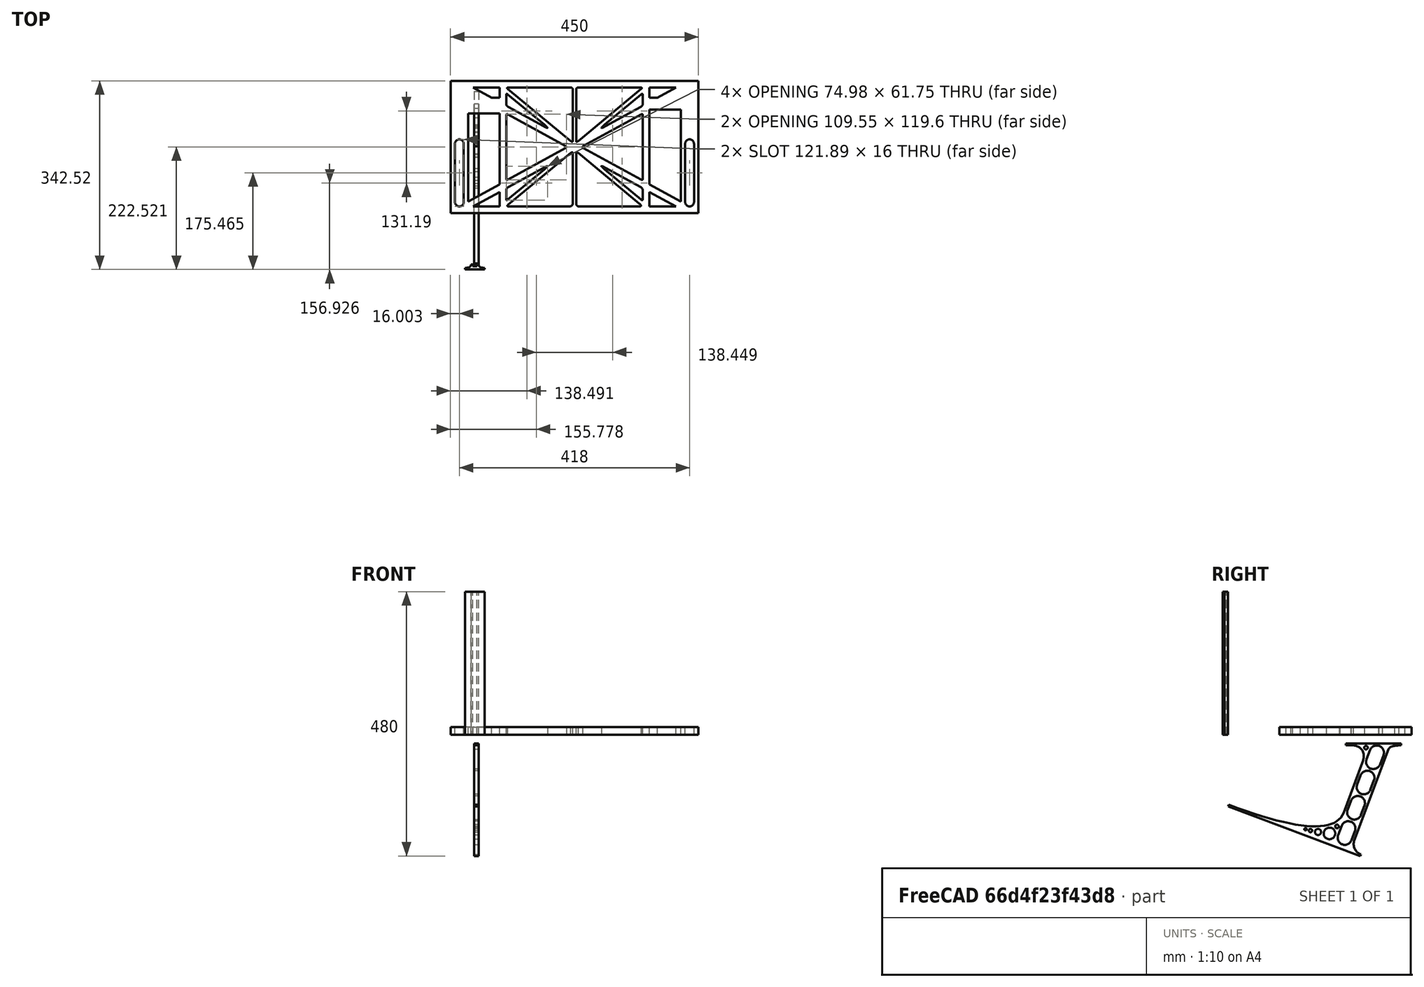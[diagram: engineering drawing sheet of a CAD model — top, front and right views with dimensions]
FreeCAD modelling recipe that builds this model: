
FCSTD DOCUMENT  (FreeCAD 0.19R0.19.2)
Label: laptopStand094
License: All rights reserved
LicenseURL: http://en.wikipedia.org/wiki/All_rights_reserved
objects: Sketcher::SketchObject×3, Part::Extrusion×3
note: 6 computed .brp shape members not serialized (recipe doc carries the construction recipe); baked Part::Feature solids carry a one-line shape summary decoded from their .brp

FEATURE [Sketcher::SketchObject] Sketch
  FullyConstrained = false
  sketch-geometry (252):
    g0: LineSegment StartX=-10.9272 StartY=-82.7794 StartZ=0 EndX=46.0728 EndY=-51.4823 EndZ=0
    g1: LineSegment StartX=366.073 StartY=-91.7794 StartZ=0 EndX=318.073 EndY=-65.424 EndZ=0
    g2: LineSegment StartX=-10.9272 StartY=77.3346 StartZ=0 EndX=-10.9272 EndY=-82.7794 EndZ=0
    g3: LineSegment StartX=375.073 StartY=-82.7794 StartZ=0 EndX=375.073 EndY=83.9235 EndZ=0
    g4: LineSegment StartX=-1.92719 StartY=-91.7794 StartZ=0 EndX=46.0728 EndY=-91.7794 EndZ=0
    g5: LineSegment StartX=318.073 StartY=124.221 StartZ=0 EndX=366.073 EndY=124.221 EndZ=0
    g6: LineSegment StartX=318.073 StartY=83.9235 StartZ=0 EndX=318.073 EndY=-51.4823 EndZ=0
    g7: LineSegment StartX=318.073 StartY=-51.4823 StartZ=0 EndX=375.073 EndY=-82.7794 EndZ=0
    g8: LineSegment StartX=318.073 StartY=-65.424 StartZ=0 EndX=318.073 EndY=-91.7794 EndZ=0
    g9: LineSegment StartX=318.073 StartY=-91.7794 StartZ=0 EndX=366.073 EndY=-91.7794 EndZ=0
    g10: LineSegment StartX=46.0728 StartY=-65.424 StartZ=0 EndX=-1.92719 EndY=-91.7794 EndZ=0
    g11: LineSegment StartX=46.0728 StartY=-65.424 StartZ=0 EndX=46.0728 EndY=-91.7794 EndZ=0
    g12: LineSegment StartX=46.0728 StartY=77.3346 StartZ=0 EndX=46.0728 EndY=-51.4823 EndZ=0
    g13: LineSegment StartX=-42.9272 StartY=136.221 StartZ=0 EndX=-42.9272 EndY=-103.779 EndZ=0
    g14: LineSegment StartX=407.073 StartY=136.221 StartZ=0 EndX=407.073 EndY=-103.779 EndZ=0
    g15: ArcOfCircle CenterX=-26.9272 CenterY=22.1087 CenterZ=0 NormalX=0 NormalY=0 NormalZ=1 AngleXU=0 Radius=8 StartAngle=1e-16 EndAngle=3.14159
    g16: ArcOfCircle CenterX=-26.9272 CenterY=-83.7794 CenterZ=0 NormalX=0 NormalY=0 NormalZ=1 AngleXU=0 Radius=8 StartAngle=3.14159 EndAngle=6.28319
    g17: LineSegment StartX=-34.9272 StartY=22.1087 StartZ=0 EndX=-34.9272 EndY=-83.7794 EndZ=0
    g18: LineSegment StartX=-18.9272 StartY=22.1087 StartZ=0 EndX=-18.9272 EndY=-83.7794 EndZ=0
    g19: ArcOfCircle CenterX=391.073 CenterY=22.1087 CenterZ=0 NormalX=0 NormalY=0 NormalZ=1 AngleXU=0 Radius=8 StartAngle=-4.4e-15 EndAngle=3.14159
    g20: LineSegment StartX=399.073 StartY=22.1087 StartZ=0 EndX=399.073 EndY=-83.7794 EndZ=0
    g21: LineSegment StartX=383.073 StartY=22.1087 StartZ=0 EndX=383.073 EndY=-83.7794 EndZ=0
    g22: ArcOfCircle CenterX=391.073 CenterY=-83.7794 CenterZ=0 NormalX=0 NormalY=0 NormalZ=1 AngleXU=0 Radius=8 StartAngle=3.14159 EndAngle=6.28319
    g23: Circle CenterX=175.022 CenterY=27.0628 CenterZ=0 NormalX=0 NormalY=0 NormalZ=1 AngleXU=0 Radius=1
    g24: Circle CenterX=179.022 CenterY=24.8665 CenterZ=0 NormalX=0 NormalY=0 NormalZ=1 AngleXU=0 Radius=1
    g25: Circle CenterX=179.022 CenterY=27.0628 CenterZ=0 NormalX=0 NormalY=0 NormalZ=1 AngleXU=0 Radius=1
    g26: BSplineCurve PolesCount=3 KnotsCount=2 Degree=2 IsPeriodic=0
    g27: GeomPoint X=175.022 Y=27.0628 Z=0
    g28: GeomPoint X=179.022 Y=27.0628 Z=0
    g29: Circle CenterX=189.124 CenterY=27.0628 CenterZ=0 NormalX=0 NormalY=0 NormalZ=1 AngleXU=0 Radius=1
    g30: Circle CenterX=185.124 CenterY=24.8665 CenterZ=0 NormalX=0 NormalY=0 NormalZ=1 AngleXU=0 Radius=1
    g31: Circle CenterX=185.124 CenterY=27.0628 CenterZ=0 NormalX=0 NormalY=0 NormalZ=1 AngleXU=0 Radius=1
    g32: BSplineCurve PolesCount=3 KnotsCount=2 Degree=2 IsPeriodic=0
    g33: GeomPoint X=189.124 Y=27.0628 Z=0
    g34: GeomPoint X=185.124 Y=27.0628 Z=0
    g35: Circle CenterX=175.022 CenterY=5.37834 CenterZ=0 NormalX=0 NormalY=0 NormalZ=1 AngleXU=0 Radius=1
    g36: Circle CenterX=179.022 CenterY=7.57463 CenterZ=0 NormalX=0 NormalY=0 NormalZ=1 AngleXU=0 Radius=1
    g37: Circle CenterX=179.022 CenterY=5.34704 CenterZ=0 NormalX=0 NormalY=0 NormalZ=1 AngleXU=0 Radius=1
    g38: BSplineCurve PolesCount=3 KnotsCount=2 Degree=2 IsPeriodic=0
    g39: GeomPoint X=175.022 Y=5.37834 Z=0
    g40: GeomPoint X=179.022 Y=5.34704 Z=0
    g41: Circle CenterX=189.124 CenterY=5.37834 CenterZ=0 NormalX=0 NormalY=0 NormalZ=1 AngleXU=0 Radius=1
    g42: Circle CenterX=185.124 CenterY=7.57463 CenterZ=0 NormalX=0 NormalY=0 NormalZ=1 AngleXU=0 Radius=1
    g43: Circle CenterX=185.124 CenterY=5.34704 CenterZ=0 NormalX=0 NormalY=0 NormalZ=1 AngleXU=0 Radius=1
    g44: BSplineCurve PolesCount=3 KnotsCount=2 Degree=2 IsPeriodic=0
    g45: GeomPoint X=189.124 Y=5.37834 Z=0
    g46: GeomPoint X=185.124 Y=5.34704 Z=0
    g47: Circle CenterX=165.871 CenterY=18.1458 CenterZ=0 NormalX=0 NormalY=0 NormalZ=1 AngleXU=0 Radius=1
    g48: Circle CenterX=169.377 CenterY=16.2206 CenterZ=0 NormalX=0 NormalY=0 NormalZ=1 AngleXU=0 Radius=1
    g49: Circle CenterX=165.871 CenterY=14.2954 CenterZ=0 NormalX=0 NormalY=0 NormalZ=1 AngleXU=0 Radius=1
    g50: BSplineCurve PolesCount=3 KnotsCount=2 Degree=2 IsPeriodic=0
    g51: GeomPoint X=165.871 Y=18.1458 Z=0
    g52: GeomPoint X=165.871 Y=14.2954 Z=0
    g53: Circle CenterX=198.275 CenterY=18.1458 CenterZ=0 NormalX=0 NormalY=0 NormalZ=1 AngleXU=0 Radius=1
    g54: Circle CenterX=194.768 CenterY=16.2206 CenterZ=0 NormalX=0 NormalY=0 NormalZ=1 AngleXU=0 Radius=1
    g55: Circle CenterX=198.275 CenterY=14.2954 CenterZ=0 NormalX=0 NormalY=0 NormalZ=1 AngleXU=0 Radius=1
    g56: BSplineCurve PolesCount=3 KnotsCount=2 Degree=2 IsPeriodic=0
    g57: GeomPoint X=198.275 Y=18.1458 Z=0
    g58: GeomPoint X=198.275 Y=14.2954 Z=0
    g59: LineSegment StartX=407.073 StartY=-103.779 StartZ=0 EndX=-42.9272 EndY=-103.779 EndZ=0
    g60: LineSegment StartX=407.073 StartY=136.221 StartZ=0 EndX=-42.9272 EndY=136.221 EndZ=0
    g61: LineSegment StartX=46.0728 StartY=77.3346 StartZ=0 EndX=-10.9272 EndY=77.3346 EndZ=0
    g62: LineSegment StartX=46.0728 StartY=105.865 StartZ=0 EndX=31.5028 EndY=105.865 EndZ=0
    g63: LineSegment StartX=46.0728 StartY=124.221 StartZ=0 EndX=46.0728 EndY=105.865 EndZ=0
    g64: LineSegment StartX=-1.92719 StartY=124.221 StartZ=0 EndX=31.5028 EndY=105.865 EndZ=0
    g65: LineSegment StartX=46.0728 StartY=124.221 StartZ=0 EndX=-1.92719 EndY=124.221 EndZ=0
    g66: LineSegment StartX=318.073 StartY=83.9235 StartZ=0 EndX=375.073 EndY=83.9235 EndZ=0
    g67: LineSegment StartX=318.073 StartY=105.865 StartZ=0 EndX=332.643 EndY=105.865 EndZ=0
    g68: LineSegment StartX=332.643 StartY=105.865 StartZ=0 EndX=366.073 EndY=124.221 EndZ=0
    g69: LineSegment StartX=318.073 StartY=124.221 StartZ=0 EndX=318.073 EndY=105.865 EndZ=0
    g70: Circle CenterX=125.607 CenterY=54.1951 CenterZ=0 NormalX=0 NormalY=0 NormalZ=1 AngleXU=0 Radius=1
    g71: Circle CenterX=139.632 CenterY=46.4944 CenterZ=0 NormalX=0 NormalY=0 NormalZ=1 AngleXU=0 Radius=1
    g72: Circle CenterX=127.326 CenterY=56.7187 CenterZ=0 NormalX=0 NormalY=0 NormalZ=1 AngleXU=0 Radius=1
    g73: BSplineCurve PolesCount=3 KnotsCount=2 Degree=2 IsPeriodic=0
    g74: GeomPoint X=125.607 Y=54.1951 Z=0
    g75: GeomPoint X=127.326 Y=56.7187 Z=0
    g76: Circle CenterX=236.821 CenterY=56.7187 CenterZ=0 NormalX=0 NormalY=0 NormalZ=1 AngleXU=0 Radius=1
    g77: Circle CenterX=224.513 CenterY=46.4944 CenterZ=0 NormalX=0 NormalY=0 NormalZ=1 AngleXU=0 Radius=1
    g78: Circle CenterX=238.538 CenterY=54.1951 CenterZ=0 NormalX=0 NormalY=0 NormalZ=1 AngleXU=0 Radius=1
    g79: BSplineCurve PolesCount=3 KnotsCount=2 Degree=2 IsPeriodic=0
    g80: GeomPoint X=236.821 Y=56.7187 Z=0
    g81: GeomPoint X=238.538 Y=54.1951 Z=0
    g82: Circle CenterX=238.538 CenterY=-21.7539 CenterZ=0 NormalX=0 NormalY=0 NormalZ=1 AngleXU=0 Radius=1
    g83: Circle CenterX=224.513 CenterY=-14.0532 CenterZ=0 NormalX=0 NormalY=0 NormalZ=1 AngleXU=0 Radius=1
    g84: Circle CenterX=236.821 CenterY=-24.2775 CenterZ=0 NormalX=0 NormalY=0 NormalZ=1 AngleXU=0 Radius=1
    g85: BSplineCurve PolesCount=3 KnotsCount=2 Degree=2 IsPeriodic=0
    g86: GeomPoint X=238.538 Y=-21.7539 Z=0
    g87: GeomPoint X=236.821 Y=-24.2775 Z=0
    g88: Circle CenterX=125.607 CenterY=-21.7539 CenterZ=0 NormalX=0 NormalY=0 NormalZ=1 AngleXU=0 Radius=1
    g89: Circle CenterX=139.632 CenterY=-14.0532 CenterZ=0 NormalX=0 NormalY=0 NormalZ=1 AngleXU=0 Radius=1
    g90: Circle CenterX=127.325 CenterY=-24.2775 CenterZ=0 NormalX=0 NormalY=0 NormalZ=1 AngleXU=0 Radius=1
    g91: BSplineCurve PolesCount=3 KnotsCount=2 Degree=2 IsPeriodic=0
    g92: GeomPoint X=125.607 Y=-21.7539 Z=0
    g93: GeomPoint X=127.325 Y=-24.2775 Z=0
    g94: Circle CenterX=302.996 CenterY=111.695 CenterZ=0 NormalX=0 NormalY=0 NormalZ=1 AngleXU=0 Radius=1
    g95: Circle CenterX=306.073 CenterY=114.251 CenterZ=0 NormalX=0 NormalY=0 NormalZ=1 AngleXU=0 Radius=1
    g96: Circle CenterX=306.073 CenterY=110.251 CenterZ=0 NormalX=0 NormalY=0 NormalZ=1 AngleXU=0 Radius=1
    g97: BSplineCurve PolesCount=3 KnotsCount=2 Degree=2 IsPeriodic=0
    g98: GeomPoint X=302.996 Y=111.695 Z=0
    g99: GeomPoint X=306.073 Y=110.251 Z=0
    g100: Circle CenterX=306.073 CenterY=95.2763 CenterZ=0 NormalX=0 NormalY=0 NormalZ=1 AngleXU=0 Radius=1
    g101: Circle CenterX=306.073 CenterY=91.2763 CenterZ=0 NormalX=0 NormalY=0 NormalZ=1 AngleXU=0 Radius=1
    g102: Circle CenterX=302.567 CenterY=89.3511 CenterZ=0 NormalX=0 NormalY=0 NormalZ=1 AngleXU=0 Radius=1
    g103: BSplineCurve PolesCount=3 KnotsCount=2 Degree=2 IsPeriodic=0
    g104: GeomPoint X=306.073 Y=95.2763 Z=0
    g105: GeomPoint X=302.567 Y=89.3511 Z=0
    g106: LineSegment StartX=306.073 StartY=110.251 StartZ=0 EndX=306.073 EndY=95.2763 EndZ=0
    g107: LineSegment StartX=302.996 StartY=111.695 StartZ=0 EndX=236.821 EndY=56.7187 EndZ=0
    g108: LineSegment StartX=238.538 StartY=54.1951 StartZ=0 EndX=302.567 EndY=89.3511 EndZ=0
    g109: Circle CenterX=61.1496 CenterY=111.695 CenterZ=0 NormalX=0 NormalY=0 NormalZ=1 AngleXU=0 Radius=1
    g110: Circle CenterX=58.0728 CenterY=114.251 CenterZ=0 NormalX=0 NormalY=0 NormalZ=1 AngleXU=0 Radius=1
    g111: Circle CenterX=58.0728 CenterY=110.251 CenterZ=0 NormalX=0 NormalY=0 NormalZ=1 AngleXU=0 Radius=1
    g112: BSplineCurve PolesCount=3 KnotsCount=2 Degree=2 IsPeriodic=0
    g113: GeomPoint X=61.1496 Y=111.695 Z=0
    g114: GeomPoint X=58.0728 Y=110.251 Z=0
    g115: Circle CenterX=61.5791 CenterY=89.3511 CenterZ=0 NormalX=0 NormalY=0 NormalZ=1 AngleXU=0 Radius=1
    g116: Circle CenterX=58.0728 CenterY=91.2763 CenterZ=0 NormalX=0 NormalY=0 NormalZ=1 AngleXU=0 Radius=1
    g117: Circle CenterX=58.0728 CenterY=95.2763 CenterZ=0 NormalX=0 NormalY=0 NormalZ=1 AngleXU=0 Radius=1
    g118: BSplineCurve PolesCount=3 KnotsCount=2 Degree=2 IsPeriodic=0
    g119: GeomPoint X=61.5791 Y=89.3511 Z=0
    g120: GeomPoint X=58.0728 Y=95.2763 Z=0
    g121: LineSegment StartX=58.0728 StartY=110.251 StartZ=0 EndX=58.0728 EndY=95.2763 EndZ=0
    g122: LineSegment StartX=61.1496 StartY=111.695 StartZ=0 EndX=127.326 EndY=56.7187 EndZ=0
    g123: LineSegment StartX=125.607 StartY=54.1951 StartZ=0 EndX=61.5791 EndY=89.3511 EndZ=0
    g124: Circle CenterX=61.5791 CenterY=-56.9099 CenterZ=0 NormalX=0 NormalY=0 NormalZ=1 AngleXU=0 Radius=1
    g125: Circle CenterX=58.0728 CenterY=-58.8351 CenterZ=0 NormalX=0 NormalY=0 NormalZ=1 AngleXU=0 Radius=1
    g126: Circle CenterX=58.0728 CenterY=-62.8351 CenterZ=0 NormalX=0 NormalY=0 NormalZ=1 AngleXU=0 Radius=1
    g127: BSplineCurve PolesCount=3 KnotsCount=2 Degree=2 IsPeriodic=0
    g128: GeomPoint X=61.5791 Y=-56.9099 Z=0
    g129: GeomPoint X=58.0728 Y=-62.8351 Z=0
    g130: Circle CenterX=58.0728 CenterY=-77.8102 CenterZ=0 NormalX=0 NormalY=0 NormalZ=1 AngleXU=0 Radius=1
    g131: Circle CenterX=58.0728 CenterY=-81.8102 CenterZ=0 NormalX=0 NormalY=0 NormalZ=1 AngleXU=0 Radius=1
    g132: Circle CenterX=61.1496 CenterY=-79.2541 CenterZ=0 NormalX=0 NormalY=0 NormalZ=1 AngleXU=0 Radius=1
    g133: BSplineCurve PolesCount=3 KnotsCount=2 Degree=2 IsPeriodic=0
    g134: GeomPoint X=58.0728 Y=-77.8102 Z=0
    g135: GeomPoint X=61.1496 Y=-79.2541 Z=0
    g136: LineSegment StartX=58.0728 StartY=-62.8351 StartZ=0 EndX=58.0728 EndY=-77.8102 EndZ=0
    g137: LineSegment StartX=61.1496 StartY=-79.2541 StartZ=0 EndX=127.325 EndY=-24.2775 EndZ=0
    g138: LineSegment StartX=125.607 StartY=-21.7539 StartZ=0 EndX=61.5791 EndY=-56.9099 EndZ=0
    g139: Circle CenterX=302.567 CenterY=-56.9099 CenterZ=0 NormalX=0 NormalY=0 NormalZ=1 AngleXU=0 Radius=1
    g140: Circle CenterX=306.073 CenterY=-58.8351 CenterZ=0 NormalX=0 NormalY=0 NormalZ=1 AngleXU=0 Radius=1
    g141: Circle CenterX=306.073 CenterY=-62.8351 CenterZ=0 NormalX=0 NormalY=0 NormalZ=1 AngleXU=0 Radius=1
    g142: BSplineCurve PolesCount=3 KnotsCount=2 Degree=2 IsPeriodic=0
    g143: GeomPoint X=302.567 Y=-56.9099 Z=0
    g144: GeomPoint X=306.073 Y=-62.8351 Z=0
    g145: Circle CenterX=302.996 CenterY=-79.2541 CenterZ=0 NormalX=0 NormalY=0 NormalZ=1 AngleXU=0 Radius=1
    g146: Circle CenterX=306.073 CenterY=-81.8102 CenterZ=0 NormalX=0 NormalY=0 NormalZ=1 AngleXU=0 Radius=1
    g147: Circle CenterX=306.073 CenterY=-77.8102 CenterZ=0 NormalX=0 NormalY=0 NormalZ=1 AngleXU=0 Radius=1
    g148: BSplineCurve PolesCount=3 KnotsCount=2 Degree=2 IsPeriodic=0
    g149: GeomPoint X=302.996 Y=-79.2541 Z=0
    g150: GeomPoint X=306.073 Y=-77.8102 Z=0
    g151: LineSegment StartX=306.073 StartY=-62.8351 StartZ=0 EndX=306.073 EndY=-77.8102 EndZ=0
    g152: LineSegment StartX=302.996 StartY=-79.2541 StartZ=0 EndX=236.821 EndY=-24.2775 EndZ=0
    g153: LineSegment StartX=238.538 StartY=-21.7539 StartZ=0 EndX=302.567 EndY=-56.9099 EndZ=0
    g154: Circle CenterX=61.6457 CenterY=-88.8112 CenterZ=0 NormalX=0 NormalY=0 NormalZ=1 AngleXU=0 Radius=1
    g155: Circle CenterX=58.0728 CenterY=-91.7794 CenterZ=0 NormalX=0 NormalY=0 NormalZ=1 AngleXU=0 Radius=1
    g156: Circle CenterX=63.9135 CenterY=-91.7794 CenterZ=0 NormalX=0 NormalY=0 NormalZ=1 AngleXU=0 Radius=1
    g157: BSplineCurve PolesCount=3 KnotsCount=2 Degree=2 IsPeriodic=0
    g158: GeomPoint X=61.6457 Y=-88.8112 Z=0
    g159: GeomPoint X=63.9135 Y=-91.7794 Z=0
    g160: Circle CenterX=179.022 CenterY=-85.8163 CenterZ=0 NormalX=0 NormalY=0 NormalZ=1 AngleXU=0 Radius=1
    g161: Circle CenterX=179.022 CenterY=-91.7794 CenterZ=0 NormalX=0 NormalY=0 NormalZ=1 AngleXU=0 Radius=1
    g162: Circle CenterX=171.895 CenterY=-91.7794 CenterZ=0 NormalX=0 NormalY=0 NormalZ=1 AngleXU=0 Radius=1
    g163: BSplineCurve PolesCount=3 KnotsCount=2 Degree=2 IsPeriodic=0
    g164: GeomPoint X=179.022 Y=-85.8163 Z=0
    g165: GeomPoint X=171.895 Y=-91.7794 Z=0
    g166: Circle CenterX=185.124 CenterY=-86.2028 CenterZ=0 NormalX=0 NormalY=0 NormalZ=1 AngleXU=0 Radius=1
    g167: Circle CenterX=185.124 CenterY=-91.7794 CenterZ=0 NormalX=0 NormalY=0 NormalZ=1 AngleXU=0 Radius=1
    g168: Circle CenterX=191.747 CenterY=-91.7794 CenterZ=0 NormalX=0 NormalY=0 NormalZ=1 AngleXU=0 Radius=1
    g169: BSplineCurve PolesCount=3 KnotsCount=2 Degree=2 IsPeriodic=0
    g170: GeomPoint X=185.124 Y=-86.2028 Z=0
    g171: GeomPoint X=191.747 Y=-91.7794 Z=0
    g172: Circle CenterX=299.888 CenterY=-86.6413 CenterZ=0 NormalX=0 NormalY=0 NormalZ=1 AngleXU=0 Radius=1
    g173: Circle CenterX=306.073 CenterY=-91.7794 CenterZ=0 NormalX=0 NormalY=0 NormalZ=1 AngleXU=0 Radius=1
    g174: Circle CenterX=298.776 CenterY=-91.7794 CenterZ=0 NormalX=0 NormalY=0 NormalZ=1 AngleXU=0 Radius=1
    g175: BSplineCurve PolesCount=3 KnotsCount=2 Degree=2 IsPeriodic=0
    g176: GeomPoint X=299.888 Y=-86.6413 Z=0
    g177: GeomPoint X=298.776 Y=-91.7794 Z=0
    g178: LineSegment StartX=189.124 StartY=5.37834 StartZ=0 EndX=299.888 EndY=-86.6413 EndZ=0
    g179: LineSegment StartX=298.776 StartY=-91.7794 StartZ=0 EndX=191.747 EndY=-91.7794 EndZ=0
    g180: LineSegment StartX=185.124 StartY=-86.2028 StartZ=0 EndX=185.124 EndY=5.34704 EndZ=0
    g181: LineSegment StartX=179.022 StartY=5.34704 StartZ=0 EndX=179.022 EndY=-85.8163 EndZ=0
    g182: LineSegment StartX=171.895 StartY=-91.7794 StartZ=0 EndX=63.9135 EndY=-91.7794 EndZ=0
    g183: LineSegment StartX=61.6457 StartY=-88.8112 StartZ=0 EndX=175.022 EndY=5.37834 EndZ=0
    g184: Circle CenterX=302.073 CenterY=124.221 CenterZ=0 NormalX=0 NormalY=0 NormalZ=1 AngleXU=0 Radius=1
    g185: Circle CenterX=306.073 CenterY=124.221 CenterZ=0 NormalX=0 NormalY=0 NormalZ=1 AngleXU=0 Radius=1
    g186: Circle CenterX=302.996 CenterY=121.665 CenterZ=0 NormalX=0 NormalY=0 NormalZ=1 AngleXU=0 Radius=1
    g187: BSplineCurve PolesCount=3 KnotsCount=2 Degree=2 IsPeriodic=0
    g188: GeomPoint X=302.073 Y=124.221 Z=0
    g189: GeomPoint X=302.996 Y=121.665 Z=0
    g190: Circle CenterX=189.124 CenterY=124.221 CenterZ=0 NormalX=0 NormalY=0 NormalZ=1 AngleXU=0 Radius=1
    g191: Circle CenterX=185.124 CenterY=124.221 CenterZ=0 NormalX=0 NormalY=0 NormalZ=1 AngleXU=0 Radius=1
    g192: Circle CenterX=185.124 CenterY=120.221 CenterZ=0 NormalX=0 NormalY=0 NormalZ=1 AngleXU=0 Radius=1
    g193: BSplineCurve PolesCount=3 KnotsCount=2 Degree=2 IsPeriodic=0
    g194: GeomPoint X=189.124 Y=124.221 Z=0
    g195: GeomPoint X=185.124 Y=120.221 Z=0
    g196: Circle CenterX=175.022 CenterY=124.221 CenterZ=0 NormalX=0 NormalY=0 NormalZ=1 AngleXU=0 Radius=1
    g197: Circle CenterX=179.022 CenterY=124.221 CenterZ=0 NormalX=0 NormalY=0 NormalZ=1 AngleXU=0 Radius=1
    g198: Circle CenterX=179.022 CenterY=120.221 CenterZ=0 NormalX=0 NormalY=0 NormalZ=1 AngleXU=0 Radius=1
    g199: BSplineCurve PolesCount=3 KnotsCount=2 Degree=2 IsPeriodic=0
    g200: GeomPoint X=175.022 Y=124.221 Z=0
    g201: GeomPoint X=179.022 Y=120.221 Z=0
    g202: Circle CenterX=62.0728 CenterY=124.221 CenterZ=0 NormalX=0 NormalY=0 NormalZ=1 AngleXU=0 Radius=1
    g203: Circle CenterX=58.0728 CenterY=124.221 CenterZ=0 NormalX=0 NormalY=0 NormalZ=1 AngleXU=0 Radius=1
    g204: Circle CenterX=61.1496 CenterY=121.665 CenterZ=0 NormalX=0 NormalY=0 NormalZ=1 AngleXU=0 Radius=1
    g205: BSplineCurve PolesCount=3 KnotsCount=2 Degree=2 IsPeriodic=0
    g206: GeomPoint X=62.0728 Y=124.221 Z=0
    g207: GeomPoint X=61.1496 Y=121.665 Z=0
    g208: LineSegment StartX=62.0728 StartY=124.221 StartZ=0 EndX=175.022 EndY=124.221 EndZ=0
    g209: LineSegment StartX=179.022 StartY=120.221 StartZ=0 EndX=179.022 EndY=27.0628 EndZ=0
    g210: LineSegment StartX=185.124 StartY=27.0628 StartZ=0 EndX=185.124 EndY=120.221 EndZ=0
    g211: LineSegment StartX=189.124 StartY=124.221 StartZ=0 EndX=302.073 EndY=124.221 EndZ=0
    g212: LineSegment StartX=302.996 StartY=121.665 StartZ=0 EndX=189.124 EndY=27.0628 EndZ=0
    g213: LineSegment StartX=175.022 StartY=27.0628 StartZ=0 EndX=61.1496 EndY=121.665 EndZ=0
    g214: Circle CenterX=61.5791 CenterY=75.4095 CenterZ=0 NormalX=0 NormalY=0 NormalZ=1 AngleXU=0 Radius=1
    g215: Circle CenterX=58.0728 CenterY=77.3346 CenterZ=0 NormalX=0 NormalY=0 NormalZ=1 AngleXU=0 Radius=1
    g216: Circle CenterX=58.0728 CenterY=73.3346 CenterZ=0 NormalX=0 NormalY=0 NormalZ=1 AngleXU=0 Radius=1
    g217: BSplineCurve PolesCount=3 KnotsCount=2 Degree=2 IsPeriodic=0
    g218: GeomPoint X=61.5791 Y=75.4095 Z=0
    g219: GeomPoint X=58.0728 Y=73.3346 Z=0
    g220: Circle CenterX=58.0728 CenterY=-40.8935 CenterZ=0 NormalX=0 NormalY=0 NormalZ=1 AngleXU=0 Radius=1
    g221: Circle CenterX=58.0728 CenterY=-44.8935 CenterZ=0 NormalX=0 NormalY=0 NormalZ=1 AngleXU=0 Radius=1
    g222: Circle CenterX=61.5791 CenterY=-42.9683 CenterZ=0 NormalX=0 NormalY=0 NormalZ=1 AngleXU=0 Radius=1
    g223: BSplineCurve PolesCount=3 KnotsCount=2 Degree=2 IsPeriodic=0
    g224: GeomPoint X=58.0728 Y=-40.8935 Z=0
    g225: GeomPoint X=61.5791 Y=-42.9683 Z=0
    g226: LineSegment StartX=61.5791 StartY=-42.9683 StartZ=0 EndX=165.871 EndY=14.2954 EndZ=0
    g227: LineSegment StartX=165.871 StartY=18.1458 StartZ=0 EndX=61.5791 EndY=75.4095 EndZ=0
    g228: LineSegment StartX=58.0728 StartY=73.3346 StartZ=0 EndX=58.0728 EndY=-40.8935 EndZ=0
    g229: Circle CenterX=302.567 CenterY=-42.9683 CenterZ=0 NormalX=0 NormalY=0 NormalZ=1 AngleXU=0 Radius=1
    g230: Circle CenterX=306.073 CenterY=-44.8935 CenterZ=0 NormalX=0 NormalY=0 NormalZ=1 AngleXU=0 Radius=1
    g231: Circle CenterX=306.073 CenterY=-40.8935 CenterZ=0 NormalX=0 NormalY=0 NormalZ=1 AngleXU=0 Radius=1
    g232: BSplineCurve PolesCount=3 KnotsCount=2 Degree=2 IsPeriodic=0
    g233: GeomPoint X=302.567 Y=-42.9683 Z=0
    g234: GeomPoint X=306.073 Y=-40.8935 Z=0
    g235: Circle CenterX=306.073 CenterY=73.3346 CenterZ=0 NormalX=0 NormalY=0 NormalZ=1 AngleXU=0 Radius=1
    g236: Circle CenterX=306.073 CenterY=77.3346 CenterZ=0 NormalX=0 NormalY=0 NormalZ=1 AngleXU=0 Radius=1
    g237: Circle CenterX=302.567 CenterY=75.4095 CenterZ=0 NormalX=0 NormalY=0 NormalZ=1 AngleXU=0 Radius=1
    g238: BSplineCurve PolesCount=3 KnotsCount=2 Degree=2 IsPeriodic=0
    g239: GeomPoint X=306.073 Y=73.3346 Z=0
    g240: GeomPoint X=302.567 Y=75.4095 Z=0
    g241: LineSegment StartX=302.567 StartY=-42.9683 StartZ=0 EndX=198.275 EndY=14.2954 EndZ=0
    g242: LineSegment StartX=198.275 StartY=18.1458 StartZ=0 EndX=302.567 EndY=75.4095 EndZ=0
    g243: LineSegment StartX=306.073 StartY=73.3346 StartZ=0 EndX=306.073 EndY=-40.8935 EndZ=0
    g244: LineSegment StartX=318.073 StartY=124.221 StartZ=0 EndX=322.073 EndY=124.221 EndZ=0
    g245: LineSegment StartX=366.073 StartY=124.221 StartZ=0 EndX=362.073 EndY=124.221 EndZ=0
    g246: LineSegment StartX=328.643 StartY=105.865 StartZ=0 EndX=332.643 EndY=105.865 EndZ=0
    g247: LineSegment StartX=335.6 StartY=105.351 StartZ=0 EndX=339.311 EndY=107.624 EndZ=0
    g248: LineSegment StartX=366.554 StartY=122.928 StartZ=0 EndX=363.62 EndY=120.771 EndZ=0
    g249: LineSegment StartX=318.073 StartY=105.865 StartZ=0 EndX=318.073 EndY=109.865 EndZ=0
    g250: LineSegment StartX=318.073 StartY=105.865 StartZ=0 EndX=322.073 EndY=105.865 EndZ=0
    g251: LineSegment StartX=318.073 StartY=124.221 StartZ=0 EndX=318.073 EndY=120.221 EndZ=0
  constraints (433):
    c: Horizontal(g4)
    c: Horizontal(g5)
    c: Coincident(g6,g7)
    c: Coincident(g8,g1)
    c: Tangent(g6,g8)
    c: Coincident(g11,g10)
    c: Coincident(g0,g12)
    c: Block(g7)
    c: Block(g3)
    c: Block(g1)
    c: Block(g8)
    c: Block(g11)
    c: Block(g10)
    c: Block(g0)
    c: Block(g2)
    c: Block(g5)
    c: Block(g9)
    c: Block(g4)
    c: Vertical(g13)
    c: Vertical(g14)
    c: Block(g14)
    c: Block(g13)
    c: Tangent(g15,g18) = 1.5708
    c: Tangent(g15,g17) = -1.5708
    c: Tangent(g17,g16) = -1.5708
    c: Tangent(g18,g16) = 1.5708
    c: Vertical(g17)
    c: Equal(g15,g16)
    c: Block(g18)
    c: Block(g17)
    c: Tangent(g19,g20) = 1.5708
    c: Tangent(g20,g22) = 1.5708
    c: Equal(g19,g22)
    c: Coincident(g21,g19)
    c: Coincident(g21,g22)
    c: Block(g20)
    c: Block(g21)
    c: Weight(g23) = 1
    c: Equal(g23,g24)
    c: Equal(g23,g25)
    c: InternalAlignment(g23,g26)
    c: InternalAlignment(g24,g26)
    c: InternalAlignment(g25,g26)
    c: InternalAlignment(g27,g26)
    c: InternalAlignment(g28,g26)
    c: Weight(g29) = 1
    c: Equal(g29,g30)
    c: Equal(g29,g31)
    c: InternalAlignment(g29,g32)
    c: InternalAlignment(g30,g32)
    c: InternalAlignment(g31,g32)
    c: InternalAlignment(g33,g32)
    c: InternalAlignment(g34,g32)
    c: Block(g32)
    c: Block(g26)
    c: Weight(g35) = 1
    c: Equal(g35,g36)
    c: Equal(g35,g37)
    c: InternalAlignment(g35,g38)
    c: InternalAlignment(g36,g38)
    c: InternalAlignment(g37,g38)
    c: InternalAlignment(g39,g38)
    c: InternalAlignment(g40,g38)
    c: Weight(g41) = 1
    c: Equal(g41,g42)
    c: Equal(g41,g43)
    c: InternalAlignment(g41,g44)
    c: InternalAlignment(g42,g44)
    c: InternalAlignment(g43,g44)
    c: InternalAlignment(g45,g44)
    c: InternalAlignment(g46,g44)
    c: Block(g44)
    c: Block(g38)
    c: Weight(g47) = 1
    c: Equal(g47,g48)
    c: Equal(g47,g49)
    c: InternalAlignment(g47,g50)
    c: InternalAlignment(g48,g50)
    c: InternalAlignment(g49,g50)
    c: InternalAlignment(g51,g50)
    c: InternalAlignment(g52,g50)
    c: Weight(g53) = 1
    c: Equal(g53,g54)
    c: Equal(g53,g55)
    c: InternalAlignment(g53,g56)
    c: InternalAlignment(g54,g56)
    c: InternalAlignment(g55,g56)
    c: InternalAlignment(g57,g56)
    c: InternalAlignment(g58,g56)
    c: Block(g50)
    c: Block(g56)
    c: Coincident(g59,g14)
    c: Coincident(g59,g13)
    c: Horizontal(g59)
    c: Distance(g59) = 450
    c: Coincident(g60,g14)
    c: Coincident(g60,g13)
    c: Horizontal(g60)
    c: Horizontal(g61)
    c: Coincident(g12,g61)
    c: Horizontal(g62)
    c: Vertical(g63)
    c: Block(g63)
    c: Block(g62)
    c: Block(g61)
    c: Distance(g63) = 18.3554
    c: Coincident(g65,g63)
    c: Coincident(g65,g64)
    c: Horizontal(g65)
    c: Block(g65)
    c: Block(g64)
    c: Coincident(g62,g64)
    c: Coincident(g2,g61)
    c: Coincident(g66,g6)
    c: Horizontal(g66)
    c: Horizontal(g67)
    c: Block(g66)
    c: Coincident(g68,g5)
    c: Coincident(g69,g5)
    c: Coincident(g69,g67)
    c: Vertical(g69)
    c: Block(g69)
    c: Coincident(g67,g68)
    c: Block(g68)
    c: Coincident(g3,g66)
    c: Weight(g70) = 1
    c: Equal(g70,g71)
    c: Equal(g70,g72)
    c: InternalAlignment(g70,g73)
    c: InternalAlignment(g71,g73)
    c: InternalAlignment(g72,g73)
    c: InternalAlignment(g74,g73)
    c: InternalAlignment(g75,g73)
    c: Block(g73)
    c: Weight(g76) = 1
    c: Equal(g76,g77)
    c: Equal(g76,g78)
    c: InternalAlignment(g76,g79)
    c: InternalAlignment(g77,g79)
    c: InternalAlignment(g78,g79)
    c: InternalAlignment(g80,g79)
    c: InternalAlignment(g81,g79)
    c: Block(g79)
    c: Weight(g82) = 1
    c: Equal(g82,g83)
    c: Equal(g82,g84)
    c: InternalAlignment(g82,g85)
    c: InternalAlignment(g83,g85)
    c: InternalAlignment(g84,g85)
    c: InternalAlignment(g86,g85)
    c: InternalAlignment(g87,g85)
    c: Block(g85)
    c: Weight(g88) = 1
    c: Equal(g88,g89)
    c: Equal(g88,g90)
    c: InternalAlignment(g88,g91)
    c: InternalAlignment(g89,g91)
    c: InternalAlignment(g90,g91)
    c: InternalAlignment(g92,g91)
    c: InternalAlignment(g93,g91)
    c: Block(g91)
    c: Weight(g94) = 1
    c: Equal(g94,g95)
    c: Equal(g94,g96)
    c: InternalAlignment(g94,g97)
    c: InternalAlignment(g95,g97)
    c: InternalAlignment(g96,g97)
    c: InternalAlignment(g98,g97)
    c: InternalAlignment(g99,g97)
    c: Weight(g100) = 1
    c: Equal(g100,g101)
    c: Equal(g100,g102)
    c: InternalAlignment(g100,g103)
    c: InternalAlignment(g101,g103)
    c: InternalAlignment(g102,g103)
    c: InternalAlignment(g104,g103)
    c: InternalAlignment(g105,g103)
    c: Block(g97)
    c: Block(g103)
    c: Coincident(g106,g97)
    c: Coincident(g106,g103)
    c: Vertical(g106)
    c: Coincident(g107,g97)
    c: Coincident(g107,g79)
    c: Coincident(g108,g79)
    c: Coincident(g108,g103)
    c: Weight(g109) = 1
    c: Equal(g109,g110)
    c: Equal(g109,g111)
    c: InternalAlignment(g109,g112)
    c: InternalAlignment(g110,g112)
    c: InternalAlignment(g111,g112)
    c: InternalAlignment(g113,g112)
    c: InternalAlignment(g114,g112)
    c: Weight(g115) = 1
    c: Equal(g115,g116)
    c: Equal(g115,g117)
    c: InternalAlignment(g115,g118)
    c: InternalAlignment(g116,g118)
    c: InternalAlignment(g117,g118)
    c: InternalAlignment(g119,g118)
    c: InternalAlignment(g120,g118)
    c: Block(g112)
    c: Block(g118)
    c: Coincident(g121,g112)
    c: Coincident(g121,g118)
    c: Vertical(g121)
    c: Coincident(g122,g112)
    c: Coincident(g122,g73)
    c: Coincident(g123,g73)
    c: Coincident(g123,g118)
    c: Weight(g124) = 1
    c: Equal(g124,g125)
    c: Equal(g124,g126)
    c: InternalAlignment(g124,g127)
    c: InternalAlignment(g125,g127)
    c: InternalAlignment(g126,g127)
    c: InternalAlignment(g128,g127)
    c: InternalAlignment(g129,g127)
    c: Weight(g130) = 1
    c: Equal(g130,g131)
    c: Equal(g130,g132)
    c: InternalAlignment(g130,g133)
    c: InternalAlignment(g131,g133)
    c: InternalAlignment(g132,g133)
    c: InternalAlignment(g134,g133)
    c: InternalAlignment(g135,g133)
    c: Block(g127)
    c: Block(g133)
    c: Coincident(g136,g127)
    c: Coincident(g136,g133)
    c: Vertical(g136)
    c: Coincident(g137,g133)
    c: Coincident(g137,g91)
    c: Coincident(g138,g91)
    c: Coincident(g138,g127)
    c: Weight(g139) = 1
    c: Equal(g139,g140)
    c: Equal(g139,g141)
    c: InternalAlignment(g139,g142)
    c: InternalAlignment(g140,g142)
    c: InternalAlignment(g141,g142)
    c: InternalAlignment(g143,g142)
    c: InternalAlignment(g144,g142)
    c: Weight(g145) = 1
    c: Equal(g145,g146)
    c: Equal(g145,g147)
    c: InternalAlignment(g145,g148)
    c: InternalAlignment(g146,g148)
    c: InternalAlignment(g147,g148)
    c: InternalAlignment(g149,g148)
    c: InternalAlignment(g150,g148)
    c: Block(g142)
    c: Block(g148)
    c: Coincident(g151,g142)
    c: Coincident(g151,g148)
    c: Vertical(g151)
    c: Coincident(g152,g148)
    c: Coincident(g152,g85)
    c: Coincident(g153,g85)
    c: Coincident(g153,g142)
    c: Weight(g154) = 1
    c: Equal(g154,g155)
    c: Equal(g154,g156)
    c: InternalAlignment(g154,g157)
    c: InternalAlignment(g155,g157)
    c: InternalAlignment(g156,g157)
    c: InternalAlignment(g158,g157)
    c: InternalAlignment(g159,g157)
    c: Weight(g160) = 1
    c: Equal(g160,g161)
    c: Equal(g160,g162)
    c: InternalAlignment(g160,g163)
    c: InternalAlignment(g161,g163)
    c: InternalAlignment(g162,g163)
    c: InternalAlignment(g164,g163)
    c: InternalAlignment(g165,g163)
    c: Weight(g166) = 1
    c: Equal(g166,g167)
    c: Equal(g166,g168)
    c: InternalAlignment(g166,g169)
    c: InternalAlignment(g167,g169)
    c: InternalAlignment(g168,g169)
    c: InternalAlignment(g170,g169)
    c: InternalAlignment(g171,g169)
    c: Weight(g172) = 1
    c: Equal(g172,g173)
    c: Equal(g172,g174)
    c: InternalAlignment(g172,g175)
    c: InternalAlignment(g173,g175)
    c: InternalAlignment(g174,g175)
    c: InternalAlignment(g176,g175)
    c: InternalAlignment(g177,g175)
    c: Block(g175)
    c: Block(g169)
    c: Block(g163)
    c: Block(g157)
    c: Coincident(g178,g44)
    c: Coincident(g178,g175)
    c: Coincident(g179,g175)
    c: Coincident(g179,g169)
    c: Horizontal(g179)
    c: Coincident(g180,g169)
    c: Coincident(g180,g44)
    c: Vertical(g180)
    c: Coincident(g181,g38)
    c: Coincident(g181,g163)
    c: Vertical(g181)
    c: Coincident(g182,g163)
    c: Coincident(g182,g157)
    c: Horizontal(g182)
    c: Coincident(g183,g157)
    c: Coincident(g183,g38)
    c: Weight(g184) = 1
    c: Equal(g184,g185)
    c: Equal(g184,g186)
    c: InternalAlignment(g184,g187)
    c: InternalAlignment(g185,g187)
    c: InternalAlignment(g186,g187)
    c: InternalAlignment(g188,g187)
    c: InternalAlignment(g189,g187)
    c: Weight(g190) = 1
    c: Equal(g190,g191)
    c: Equal(g190,g192)
    c: InternalAlignment(g190,g193)
    c: InternalAlignment(g191,g193)
    c: InternalAlignment(g192,g193)
    c: InternalAlignment(g194,g193)
    c: InternalAlignment(g195,g193)
    c: Weight(g196) = 1
    c: Equal(g196,g197)
    c: Equal(g196,g198)
    c: InternalAlignment(g196,g199)
    c: InternalAlignment(g197,g199)
    c: InternalAlignment(g198,g199)
    c: InternalAlignment(g200,g199)
    c: InternalAlignment(g201,g199)
    c: Weight(g202) = 1
    c: Equal(g202,g203)
    c: Equal(g202,g204)
    c: InternalAlignment(g202,g205)
    c: InternalAlignment(g203,g205)
    c: InternalAlignment(g204,g205)
    c: InternalAlignment(g206,g205)
    c: InternalAlignment(g207,g205)
    c: Block(g205)
    c: Block(g199)
    c: Block(g193)
    c: Block(g187)
    c: Coincident(g208,g205)
    c: Coincident(g208,g199)
    c: Horizontal(g208)
    c: Coincident(g209,g199)
    c: Coincident(g209,g26)
    c: Vertical(g209)
    c: Coincident(g210,g32)
    c: Coincident(g210,g193)
    c: Vertical(g210)
    c: Coincident(g211,g193)
    c: Coincident(g211,g187)
    c: Horizontal(g211)
    c: Coincident(g212,g187)
    c: Coincident(g212,g32)
    c: Coincident(g213,g26)
    c: Coincident(g213,g205)
    c: Weight(g214) = 1
    c: Equal(g214,g215)
    c: Equal(g214,g216)
    c: InternalAlignment(g214,g217)
    c: InternalAlignment(g215,g217)
    c: InternalAlignment(g216,g217)
    c: InternalAlignment(g218,g217)
    c: InternalAlignment(g219,g217)
    c: Weight(g220) = 1
    c: Equal(g220,g221)
    c: Equal(g220,g222)
    c: InternalAlignment(g220,g223)
    c: InternalAlignment(g221,g223)
    c: InternalAlignment(g222,g223)
    c: InternalAlignment(g224,g223)
    c: InternalAlignment(g225,g223)
    c: Block(g223)
    c: Block(g217)
    c: Coincident(g226,g223)
    c: Coincident(g226,g50)
    c: Coincident(g227,g50)
    c: Coincident(g227,g217)
    c: Coincident(g228,g217)
    c: Coincident(g228,g223)
    c: Vertical(g228)
    c: Weight(g229) = 1
    c: Equal(g229,g230)
    c: Equal(g229,g231)
    c: InternalAlignment(g229,g232)
    c: InternalAlignment(g230,g232)
    c: InternalAlignment(g231,g232)
    c: InternalAlignment(g233,g232)
    c: InternalAlignment(g234,g232)
    c: Weight(g235) = 1
    c: Equal(g235,g236)
    c: Equal(g235,g237)
    c: InternalAlignment(g235,g238)
    c: InternalAlignment(g236,g238)
    c: InternalAlignment(g237,g238)
    c: InternalAlignment(g239,g238)
    c: InternalAlignment(g240,g238)
    c: Block(g238)
    c: Block(g232)
    c: Coincident(g241,g232)
    c: Coincident(g241,g56)
    c: Coincident(g242,g56)
    c: Coincident(g242,g238)
    c: Coincident(g243,g238)
    c: Coincident(g243,g232)
    c: Vertical(g243)
    c: Horizontal(g244)
    c: Horizontal(g245)
    c: Horizontal(g246)
    c: Vertical(g249)
    c: Horizontal(g250)
    c: Vertical(g251)
    c: Distance(g246) = 4
    c: Distance(g250) = 4
    c: Distance(g249) = 4
    c: Distance(g251) = 4
    c: Distance(g244) = 4
    c: Distance(g245) = 4
    c: Coincident(g244,g5)
    c: Coincident(g251,g5)
    c: Coincident(g249,g67)
    c: Coincident(g250,g67)
    c: Coincident(g246,g67)
    c: Coincident(g5,g245)
FEATURE [Sketcher::SketchObject] Sketch001
  FullyConstrained = true
  MapMode = 4
  Placement = pos=(0,0,0) rot=(0.57735,0.57735,0.57735;2.0944rad)
  Support = -> [Sketch]
  sketch-geometry (46):
    g0: BSplineCurve PolesCount=3 KnotsCount=2 Degree=2 IsPeriodic=0
    g1: ArcOfCircle CenterX=73.1223 CenterY=-32.291 CenterZ=0 NormalX=0 NormalY=0 NormalZ=1 AngleXU=0 Radius=13 StartAngle=5.92268 EndAngle=9.06428
    g2: ArcOfCircle CenterX=66.7816 CenterY=-49.1439 CenterZ=0 NormalX=0 NormalY=0 NormalZ=1 AngleXU=0 Radius=13 StartAngle=2.78068 EndAngle=5.92131
    g3: ArcOfCircle CenterX=55.9263 CenterY=-78.1807 CenterZ=0 NormalX=0 NormalY=0 NormalZ=1 AngleXU=0 Radius=13 StartAngle=5.92268 EndAngle=9.06428
    g4: ArcOfCircle CenterX=49.5884 CenterY=-95.0342 CenterZ=0 NormalX=0 NormalY=0 NormalZ=1 AngleXU=0 Radius=13 StartAngle=2.78068 EndAngle=5.92131
    g5: ArcOfCircle CenterX=38.7206 CenterY=-124.067 CenterZ=0 NormalX=0 NormalY=0 NormalZ=1 AngleXU=0 Radius=13 StartAngle=5.92268 EndAngle=9.06428
    g6: ArcOfCircle CenterX=32.3875 CenterY=-140.92 CenterZ=0 NormalX=0 NormalY=0 NormalZ=1 AngleXU=0 Radius=13 StartAngle=2.78068 EndAngle=5.92131
    g7: ArcOfCircle CenterX=21.4715 CenterY=-169.934 CenterZ=0 NormalX=0 NormalY=0 NormalZ=1 AngleXU=0 Radius=13 StartAngle=5.92268 EndAngle=9.06428
    g8: ArcOfCircle CenterX=15.1336 CenterY=-186.787 CenterZ=0 NormalX=0 NormalY=0 NormalZ=1 AngleXU=0 Radius=13 StartAngle=2.78068 EndAngle=5.92131
    g9-g12: Circle x4 (B-spline internal-alignment scaffolding for g13; pole/knot coordinates omitted)
    g13: BSplineCurve PolesCount=4 KnotsCount=2 Degree=3 IsPeriodic=0
    g14: GeomPoint X=28.8094 Y=-19.0875 Z=0
    g15: GeomPoint X=47.0443 Y=-50.4712 Z=0
    g16: Circle CenterX=53.5586 CenterY=-23.2695 CenterZ=0 NormalX=0 NormalY=0 NormalZ=1 AngleXU=0 Radius=3.24518
    g17: Circle CenterX=-195.441 CenterY=-127.082 CenterZ=0 NormalX=0 NormalY=0 NormalZ=1 AngleXU=0 Radius=1
    g18: Circle CenterX=-8.24091 CenterY=-197.481 CenterZ=0 NormalX=0 NormalY=0 NormalZ=1 AngleXU=0 Radius=1
    g19: Circle CenterX=12.8789 CenterY=-141.321 CenterZ=0 NormalX=0 NormalY=0 NormalZ=1 AngleXU=0 Radius=1
    g20: BSplineCurve PolesCount=3 KnotsCount=2 Degree=2 IsPeriodic=0
    g21: GeomPoint X=-195.441 Y=-127.082 Z=0
    g22: GeomPoint X=12.8789 Y=-141.321 Z=0
    g23: Circle CenterX=-12.8016 CenterY=-179.036 CenterZ=0 NormalX=0 NormalY=0 NormalZ=1 AngleXU=0 Radius=10.5072
    g24: Circle CenterX=0.933922 CenterY=-166.43 CenterZ=0 NormalX=0 NormalY=0 NormalZ=1 AngleXU=0 Radius=3.26661
    g25: Circle CenterX=-33.5518 CenterY=-176.44 CenterZ=0 NormalX=0 NormalY=0 NormalZ=1 AngleXU=0 Radius=5.64388
    g26: Circle CenterX=-47.2366 CenterY=-173.859 CenterZ=0 NormalX=0 NormalY=0 NormalZ=1 AngleXU=0 Radius=3.01653
    g27: Circle CenterX=-56.2595 CenterY=-171.456 CenterZ=0 NormalX=0 NormalY=0 NormalZ=1 AngleXU=0 Radius=2.12826
    g28: ArcOfCircle CenterX=51.2151 CenterY=-198.473 CenterZ=0 NormalX=0 NormalY=0 NormalZ=1 AngleXU=0 Radius=20 StartAngle=2.78189 EndAngle=4.35269
    g29: LineSegment StartX=32.4951 StartY=-191.433 StartZ=0 EndX=94.6578 EndY=-26.1352 EndZ=0
    g30: LineSegment StartX=43.1192 StartY=-220.001 StartZ=0 EndX=-196.497 EndY=-129.89 EndZ=0
    g31: LineSegment StartX=43.1192 StartY=-220.001 StartZ=0 EndX=44.1752 EndY=-217.193 EndZ=0
    g32: LineSegment StartX=117.223 StartY=-19.0875 StartZ=0 EndX=117.223 EndY=-16.0875 EndZ=0
    g33: LineSegment StartX=117.223 StartY=-16.0875 StartZ=0 EndX=17.2232 EndY=-16.0875 EndZ=0
    g34: LineSegment StartX=17.2232 StartY=-16.0875 StartZ=0 EndX=17.2232 EndY=-19.0875 EndZ=0
    g35: LineSegment StartX=28.8094 StartY=-19.0875 StartZ=0 EndX=17.2232 EndY=-19.0875 EndZ=0
    g36: LineSegment StartX=47.0443 StartY=-50.4712 StartZ=0 EndX=12.8789 EndY=-141.321 EndZ=0
    g37: LineSegment StartX=-195.441 StartY=-127.082 StartZ=0 EndX=-196.497 EndY=-129.89 EndZ=0
    g38: LineSegment StartX=85.2866 StartY=-36.8766 StartZ=0 EndX=78.9396 EndY=-53.7463 EndZ=0
    g39: LineSegment StartX=60.9579 StartY=-27.7053 StartZ=0 EndX=54.6191 EndY=-44.5532 EndZ=0
    g40: LineSegment StartX=68.0907 StartY=-82.7664 StartZ=0 EndX=61.7465 EndY=-99.6365 EndZ=0
    g41: LineSegment StartX=43.7619 StartY=-73.595 StartZ=0 EndX=37.426 EndY=-90.4435 EndZ=0
    g42: LineSegment StartX=50.885 StartY=-128.652 StartZ=0 EndX=44.5456 EndY=-145.522 EndZ=0
    g43: LineSegment StartX=26.5562 StartY=-119.481 StartZ=0 EndX=20.2251 EndY=-136.329 EndZ=0
    g44: LineSegment StartX=9.3071 StartY=-165.349 StartZ=0 EndX=2.97115 EndY=-182.197 EndZ=0
    g45: LineSegment StartX=33.6358 StartY=-174.52 StartZ=0 EndX=27.2917 EndY=-191.39 EndZ=0
  constraints (71):
    c: Block(g0)
    c: Block(g1)
    c: Block(g2)
    c: Block(g4)
    c: Block(g3)
    c: Block(g6)
    c: Block(g5)
    c: Block(g8)
    c: Block(g7)
    c: Weight(g9) = 1
    c: Equal(g9,g10)
    c: Equal(g9,g11)
    c: Equal(g9,g12)
    c: InternalAlignment(g9-g12 -> g13) x4
    c: InternalAlignment(g14,g13)
    c: InternalAlignment(g15,g13)
    c: Block(g16)
    c: Weight(g17) = 1
    c: Equal(g17,g18)
    c: Equal(g17,g19)
    c: InternalAlignment(g17,g20)
    c: InternalAlignment(g18,g20)
    c: InternalAlignment(g19,g20)
    c: InternalAlignment(g21,g20)
    c: InternalAlignment(g22,g20)
    c: Block(g20)
    c: Block(g23)
    c: Block(g24)
    c: Block(g25)
    c: Block(g26)
    c: Block(g27)
    c: Block(g28)
    c: Coincident(g29,g28)
    c: Coincident(g29,g0)
    c: Block(g13)
    c: Coincident(g31,g30)
    c: Coincident(g31,g28)
    c: Block(g31)
    c: Coincident(g32,g0)
    c: Vertical(g32)
    c: Coincident(g33,g32)
    c: Horizontal(g33)
    c: Coincident(g34,g33)
    c: Vertical(g34)
    c: Block(g33)
    c: Coincident(g35,g13)
    c: Coincident(g35,g34)
    c: Horizontal(g35)
    c: Coincident(g36,g13)
    c: Coincident(g36,g20)
    c: Coincident(g37,g20)
    c: Coincident(g37,g30)
    c: Block(g30)
    c: Coincident(g38,g1)
    c: Coincident(g38,g2)
    c: Coincident(g39,g1)
    c: Coincident(g39,g2)
    c: Coincident(g40,g3)
    c: Coincident(g40,g4)
    c: Coincident(g41,g3)
    c: Coincident(g41,g4)
    c: Coincident(g42,g5)
    c: Coincident(g42,g6)
    c: Coincident(g43,g5)
    c: Coincident(g43,g6)
    c: Coincident(g44,g7)
    c: Coincident(g44,g8)
    c: Coincident(g45,g7)
    c: Coincident(g45,g8)
    c: Distance(g30) = 256
    c: Distance(g33) = 100
FEATURE [Part::Extrusion] Extrude002
  Base = -> Sketch001
  Dir = (1,0,0)
  DirMode = 2
  FaceMakerClass = Part::FaceMakerBullseye
  LengthFwd = 8
  LengthRev = 0
  Solid = true
  Symmetric = false
FEATURE [Sketcher::SketchObject] Sketch002
  FullyConstrained = true
  sketch-geometry (20):
    g0: LineSegment StartX=-2.77179 StartY=-200.304 StartZ=0 EndX=5.22821 EndY=-200.304 EndZ=0
    g1: LineSegment StartX=5.22821 StartY=-200.304 StartZ=0 EndX=5.22821 EndY=-197.304 EndZ=0
    g2: LineSegment StartX=-2.77179 StartY=-200.304 StartZ=0 EndX=-2.77179 EndY=-197.304 EndZ=0
    g3: LineSegment StartX=5.22821 StartY=-197.304 StartZ=0 EndX=8.22821 EndY=-197.304 EndZ=0
    g4: LineSegment StartX=-2.77179 StartY=-197.304 StartZ=0 EndX=-5.77179 EndY=-197.304 EndZ=0
    g5: LineSegment StartX=19.2282 StartY=-203.304 StartZ=0 EndX=19.2282 EndY=-206.304 EndZ=0
    g6: LineSegment StartX=-16.7718 StartY=-203.304 StartZ=0 EndX=-16.7718 EndY=-206.304 EndZ=0
    g7: LineSegment StartX=-16.7718 StartY=-206.304 StartZ=0 EndX=19.2282 EndY=-206.304 EndZ=0
    g8: Circle CenterX=-16.7718 CenterY=-203.304 CenterZ=0 NormalX=0 NormalY=0 NormalZ=1 AngleXU=0 Radius=1
    g9: Circle CenterX=-5.77179 CenterY=-203.304 CenterZ=0 NormalX=0 NormalY=0 NormalZ=1 AngleXU=0 Radius=1
    g10: Circle CenterX=-5.77179 CenterY=-197.304 CenterZ=0 NormalX=0 NormalY=0 NormalZ=1 AngleXU=0 Radius=1
    g11: BSplineCurve PolesCount=3 KnotsCount=2 Degree=2 IsPeriodic=0
    g12: GeomPoint X=-16.7718 Y=-203.304 Z=0
    g13: GeomPoint X=-5.77179 Y=-197.304 Z=0
    g14: Circle CenterX=19.2282 CenterY=-203.304 CenterZ=0 NormalX=0 NormalY=0 NormalZ=1 AngleXU=0 Radius=1
    g15: Circle CenterX=8.22821 CenterY=-203.304 CenterZ=0 NormalX=0 NormalY=0 NormalZ=1 AngleXU=0 Radius=1
    g16: Circle CenterX=8.22821 CenterY=-197.304 CenterZ=0 NormalX=0 NormalY=0 NormalZ=1 AngleXU=0 Radius=1
    g17: BSplineCurve PolesCount=3 KnotsCount=2 Degree=2 IsPeriodic=0
    g18: GeomPoint X=19.2282 Y=-203.304 Z=0
    g19: GeomPoint X=8.22821 Y=-197.304 Z=0
  constraints (41):
    c: Horizontal(g0)
    c: Distance(g0) = 8
    c: Coincident(g1,g0)
    c: Vertical(g1)
    c: Distance(g1) = 3
    c: Coincident(g2,g0)
    c: Vertical(g2)
    c: Distance(g2) = 3
    c: Coincident(g3,g1)
    c: Horizontal(g3)
    c: Distance(g3) = 3
    c: Coincident(g4,g2)
    c: Horizontal(g4)
    c: Distance(g4) = 3
    c: Vertical(g5)
    c: Vertical(g6)
    c: Coincident(g7,g6)
    c: Coincident(g7,g5)
    c: Weight(g8) = 1
    c: Equal(g8,g9)
    c: Equal(g8,g10)
    c: Coincident(g11,g4)
    c: InternalAlignment(g8,g11)
    c: InternalAlignment(g9,g11)
    c: InternalAlignment(g10,g11)
    c: InternalAlignment(g12,g11)
    c: InternalAlignment(g13,g11)
    c: Coincident(g17,g5)
    c: Weight(g14) = 1
    c: Equal(g14,g15)
    c: Equal(g14,g16)
    c: Coincident(g17,g3)
    c: InternalAlignment(g14,g17)
    c: InternalAlignment(g15,g17)
    c: InternalAlignment(g16,g17)
    c: InternalAlignment(g18,g17)
    c: InternalAlignment(g19,g17)
    c: Block(g7)
    c: Block(g17)
    c: Block(g11)
    c: Block(g6)
FEATURE [Part::Extrusion] Extrude003
  Base = -> Sketch002
  Dir = (0,0,1)
  DirMode = 2
  FaceMakerClass = Part::FaceMakerBullseye
  LengthFwd = 260
  LengthRev = 0
  Solid = true
  Symmetric = false
FEATURE [Part::Extrusion] Extrude
  Base = -> Sketch
  Dir = (0,0,1)
  DirMode = 2
  FaceMakerClass = Part::FaceMakerBullseye
  LengthFwd = 14
  LengthRev = 0
  Solid = true
  Symmetric = false
